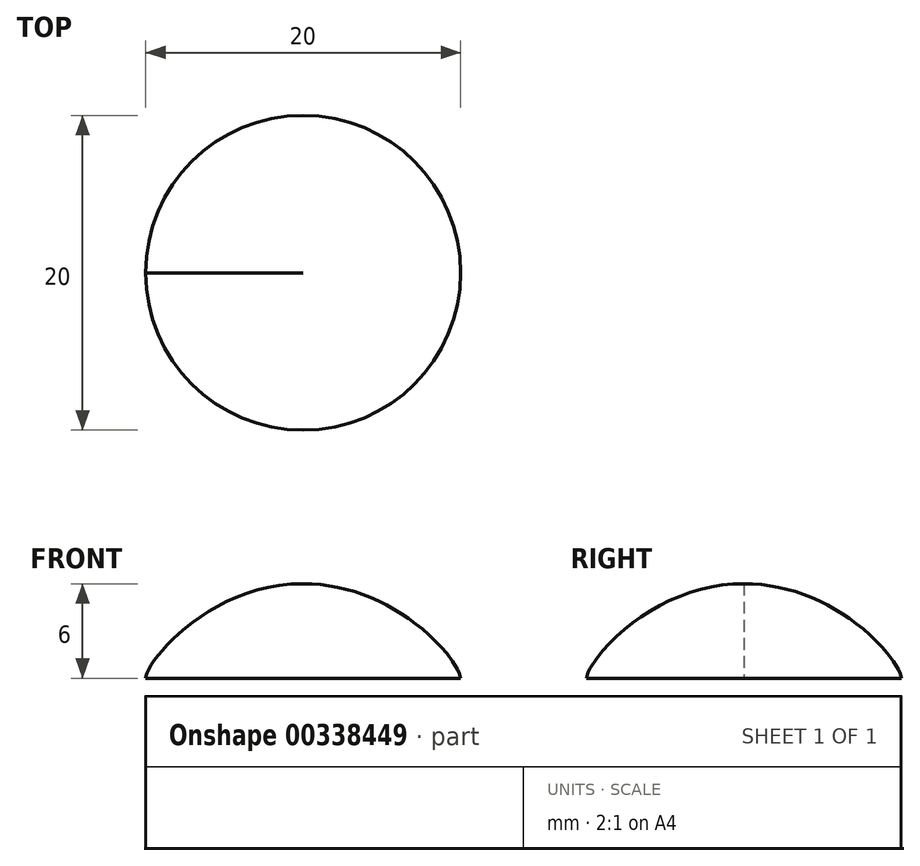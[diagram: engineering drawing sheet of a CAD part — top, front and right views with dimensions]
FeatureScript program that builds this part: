
annotation { "Feature Type Name" : "Feature", "Feature Type Description" : "" }
export const myFeature = defineFeature(function(context is Context, id is Id, definition is map)
    precondition{}
    {
        {
            var Q0;
            Q0=qCreatedBy(makeId("Front.planeOp"),FACE);
            var sketch = newSketch(context, id + "F0", { "sketchPlane" : qUnion([Q0])});
            skLineSegment(sketch, "E0", {"start": v(0, 0) * mm, "end": v(-10, 0) * mm});
            skLineSegment(sketch, "E1", {"start": v(0, 0) * mm, "end": v(0, 6) * mm});
            skFitSpline(sketch, "E2", {"points": [v(0, 6) * mm, v(-10, 0) * mm], "startDerivative": vector(-18, 0) * mm, "endDerivative": vector(0, -3) * mm});
            skSolve(sketch);
        }
        {
            var Q0;
            Q0=makeQuery(id+"F0.imprint","IMPRINT",FACE,{"disambiguationData":[TD([[makeQuery(id+"F0.imprint","IMPRINT",EDGE,{"derivedFrom":sQuery(id+"F0.wireOp",EDGE,"E0")}),-1.0]])]});
            var Q1;
            Q1=sQuery(id+"F0.wireOp",EDGE,"E1");
            revolve(context, id + "F1", {"surfaceOperationType" : NewSurfaceOperationType.NEW, "entities" : qUnion([Q0]), "axis" : qUnion([Q1]), "revolveType" : RevolveType.FULL});
        }
    });
